# Revit family: Drain-Green_Roof-Jay R. Smith-Round_Type-1900_Series (aa6b9991-9b21-4e79-a296-04797d5d9b2e) (1)
name_source: partatom
category: Plumbing Fixtures
units: mm (PartAtom-declared; Revit-internal decimal feet)

## family parameters
Always vertical = Yes
Cut with Voids When Loaded = No
OmniClass Number = 23.70.50.21.24.11
OmniClass Title = Roof Waste Water Drains
Part Type = Normal
Room Calculation Point = No
Round Connector Dimension = Use Radius
Shared = No
Work Plane-Based = Yes

## types (18) — shared parameters
Assembly Code = D2040200
Body Material = Cast Iron-Jay R Smith-Duco Coated
C - Underdeck Clamp = No
CL - "L" Shaped Underdeck Clamp = No
CW Connection = No
Default Elevation = 0"
Description = Green Roof Main Area Drain with Standpipe
Diameter = 15 1/4"
G - Galvanized Cast Iron = No
Gravel Guard Material = Stainless Steel-Jay R Smith-Perforated
HW Connection = No
Installation Type = Deck Mounted
L - Speedi-Set Service Weight - 02"(50), 03"(75) & 04"(100) sizes only = No
LXH - Speedi-Set Extra Heavy - 02"(50), 03"(75) & 04"(100) sizes only = No
Load Rating = Load between 2,000 lbs. (900 kg) and 4,999 lbs. (2,250 kg) per ASME A112.6.3
Floor Drain Standard.
Manufacturer = Jay R. Smith
Material = Cast Iron-Jay R Smith-Duco Coated
Overall Diameter = 15 1/4"
Perforated Gravel Stop Height = 18"
Perforated P.V.C. Standpipe Height = 16 1/2"
Product Documentation Link = https://www.jrsmith.com
Product Page URL = https://www.jrsmith.com
R - Sump Receiver = No
Standpipe Material = Plastic-Jay R Smith-White
URL = http://www.jrsmith.com
Vent Connection = No
Waste Connection = Yes

## per-type parameters (varying)
| type | B Dimension | B Dimension/2 | Connection Outlet Description | Depth Of Body | Outlet Diameter | Outlet Radius | T - Threaded Outlet |
| 1900C02 | 4" | 2" | 2" Caulk Outlet Connection | 5" | 2" | 1" | No |
| 1900C03 | 4" | 2" | 3" Caulk Outlet Connection | 5" | 3" | 1 1/2" | No |
| 1900C04 | 4" | 2" | 4" Caulk Outlet Connection | 5" | 4" | 2" | No |
| 1900C05 | 6" | 3" | 5" Caulk Outlet Connection | 5" | 5" | 2 1/2" | No |
| 1900C06 | 6" | 3" | 6" Caulk Outlet Connection | 5" | 6" | 3" | No |
| 1900C08 | 8" | 4" | 8" Caulk Outlet Connection | 5" | 8" | 4" | No |
| 1900Y02 | 4" | 2" | 2" No-HUB Outlet Connection | 5" | 2" | 1" | No |
| 1900Y03 | 4" | 2" | 3" No-HUB Outlet Connection | 5" | 3" | 1 1/2" | No |
| 1900Y04 | 4" | 2" | 4" No-HUB Outlet Connection | 5" | 4" | 2" | No |
| 1900Y05 | 6" | 3" | 5" No-HUB Outlet Connection | 5" | 5" | 2 1/2" | No |
| 1900Y06 | 6" | 3" | 6" No-HUB Outlet Connection | 5" | 6" | 3" | No |
| 1900Y08 | 8" | 4" | 8" No-HUB Outlet Connection | 5" | 8" | 4" | No |
| 1900T02 | 4" | 2" | 2" Threaded Outlet Connection | 3 3/4" | 2" | 1" | Yes |
| 1900T03 | 4" | 2" | 3" Threaded Outlet Connection | 3 3/4" | 3" | 1 1/2" | Yes |
| 1900T04 | 4" | 2" | 4" Threaded Outlet Connection | 3 3/4" | 4" | 2" | Yes |
| 1900T05 | 6" | 3" | 5" Threaded Outlet Connection | 3 3/4" | 5" | 2 1/2" | Yes |
| 1900T06 | 6" | 3" | 6" Threaded Outlet Connection | 3 3/4" | 6" | 3" | Yes |
| 1900T08 | 8" | 4" | 8" Threaded Outlet Connection | 3 3/4" | 8" | 4" | Yes |

note: column(s) folded — value = type name in every type: Model

## geometry (parser evidence)
native form markers: Sweep x3
no freeform markers — native parametric forms only
